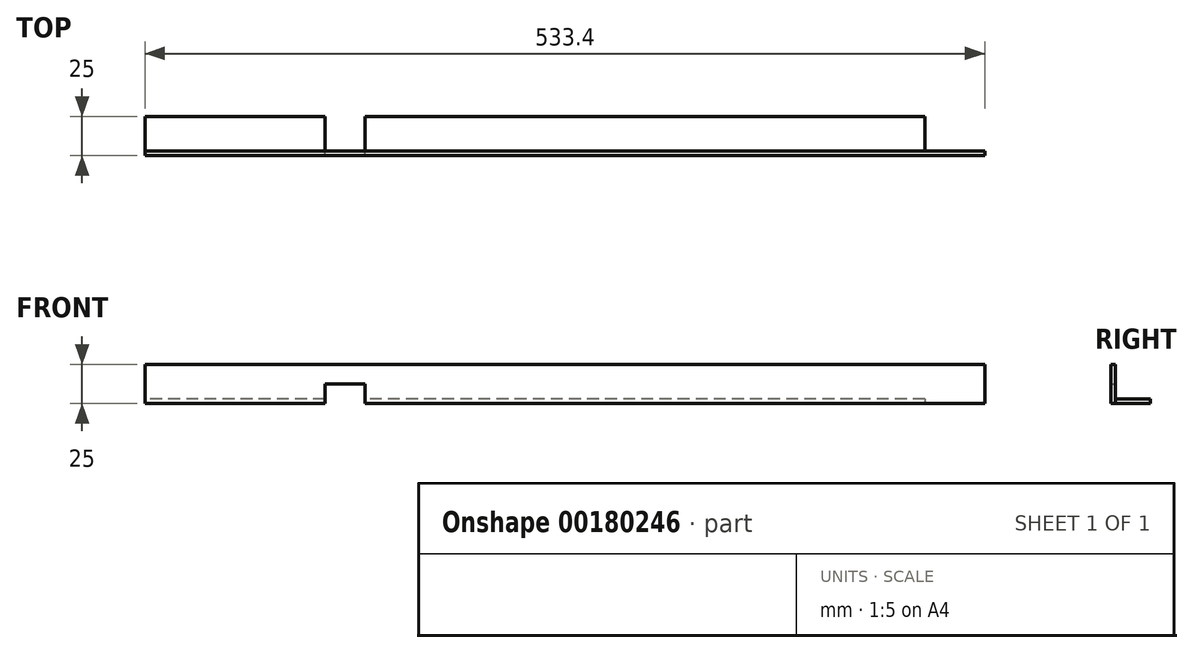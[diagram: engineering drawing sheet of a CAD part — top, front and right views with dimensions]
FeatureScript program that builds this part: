
annotation { "Feature Type Name" : "Feature", "Feature Type Description" : "" }
export const myFeature = defineFeature(function(context is Context, id is Id, definition is map)
    precondition{}
    {
        {
            var Q0;
            Q0=qCreatedBy(makeId("Right.planeOp"),FACE);
            var sketch = newSketch(context, id + "F0", { "sketchPlane" : qUnion([Q0])});
            skLineSegment(sketch, "E0", {"start": v(0, 0) * mm, "end": v(25, 0) * mm});
            skLineSegment(sketch, "E1", {"start": v(0, 0) * mm, "end": v(0, 25) * mm});
            skLineSegment(sketch, "E2.0", {"start": v(3, 3) * mm, "end": v(3, 25) * mm});
            skLineSegment(sketch, "E3.0", {"start": v(3, 3) * mm, "end": v(25, 3) * mm});
            skLineSegment(sketch, "E4", {"start": v(0, 25) * mm, "end": v(3, 25) * mm});
            skLineSegment(sketch, "E5", {"start": v(25, 3) * mm, "end": v(25, 0) * mm});
            skLineSegment(sketch, "E6.filletArc", {"start": v(3, 3) * mm, "end": v(3, 3) * mm});
            skSolve(sketch);
        }
        {
            var Q0;
            Q0=makeQuery(id+"F0.imprint","IMPRINT",FACE,{"disambiguationData":[TD([[makeQuery(id+"F0.imprint","IMPRINT",EDGE,{"derivedFrom":sQuery(id+"F0.wireOp",EDGE,"E0")}),1.0]])]});
            extrude(context, id + "F1", {"entities" : qUnion([Q0]), "depth" : 533.4 * mm});
        }
        {
            var Q0;
            Q0=qCreatedBy(makeId("Right.planeOp"),FACE);
            cPlane(context, id + "F2", {"entities" : qUnion([Q0]), "cplaneType" : CPlaneType.OFFSET, "offset" : 114.3 * mm, "width" : 150 * mm, "height" : 150 * mm});
        }
        {
            var Q0;
            Q0=qCreatedBy(id+"F2.planeOp",FACE);
            var sketch = newSketch(context, id + "F3", { "sketchPlane" : qUnion([Q0])});
            skLineSegment(sketch, "E7.0", {"start": v(0, 0) * mm, "end": v(25, 0) * mm});
            skLineSegment(sketch, "E7.1", {"start": v(0, 0) * mm, "end": v(0, 12.5) * mm});
            skLineSegment(sketch, "E7.2", {"start": v(3, 3) * mm, "end": v(3, 12.5) * mm});
            skLineSegment(sketch, "E7.3", {"start": v(3, 3) * mm, "end": v(25, 3) * mm});
            skLineSegment(sketch, "E7.5", {"start": v(25, 3) * mm, "end": v(25, 0) * mm});
            skLineSegment(sketch, "E8.0", {"start": v(0, 12.5) * mm, "end": v(3, 12.5) * mm});
            skSolve(sketch);
        }
        {
            var Q0;
            Q0=makeQuery(id+"F3.imprint","IMPRINT",FACE,{"disambiguationData":[TD([[makeQuery(id+"F3.imprint","IMPRINT",EDGE,{"derivedFrom":sQuery(id+"F3.wireOp",EDGE,"E7.0")}),1.0]])]});
            extrude(context, id + "F4", {"entities" : qUnion([Q0]), "operationType" : NewBodyOperationType.REMOVE, "depth" : 25.4 * mm});
        }
        {
            var Q0;
            Q0=qCreatedBy(makeId("Right.planeOp"),FACE);
            cPlane(context, id + "F5", {"entities" : qUnion([Q0]), "cplaneType" : CPlaneType.OFFSET, "offset" : 533.4 * mm, "width" : 150 * mm, "height" : 150 * mm});
        }
        {
            var Q0;
            Q0=qCreatedBy(id+"F5.planeOp",FACE);
            var sketch = newSketch(context, id + "F6", { "sketchPlane" : qUnion([Q0])});
            skLineSegment(sketch, "E9.0", {"start": v(25, 3) * mm, "end": v(25, 0) * mm});
            skLineSegment(sketch, "E9.1", {"start": v(3, 0) * mm, "end": v(25, 0) * mm});
            skLineSegment(sketch, "E9.3", {"start": v(3, 0) * mm, "end": v(3, 3) * mm});
            skLineSegment(sketch, "E9.4", {"start": v(3, 3) * mm, "end": v(25, 3) * mm});
            skPoint(sketch, "E10.orphan", {"position": v(3, 3) * mm});
            skSolve(sketch);
        }
        {
            var Q0;
            Q0=makeQuery(id+"F6.imprint","IMPRINT",FACE,{"disambiguationData":[TD([[makeQuery(id+"F6.imprint","IMPRINT",EDGE,{"derivedFrom":sQuery(id+"F6.wireOp",EDGE,"E9.0")}),-1.0]])]});
            extrude(context, id + "F7", {"entities" : qUnion([Q0]), "operationType" : NewBodyOperationType.REMOVE, "oppositeDirection" : true, "depth" : 38.1 * mm});
        }
    });
